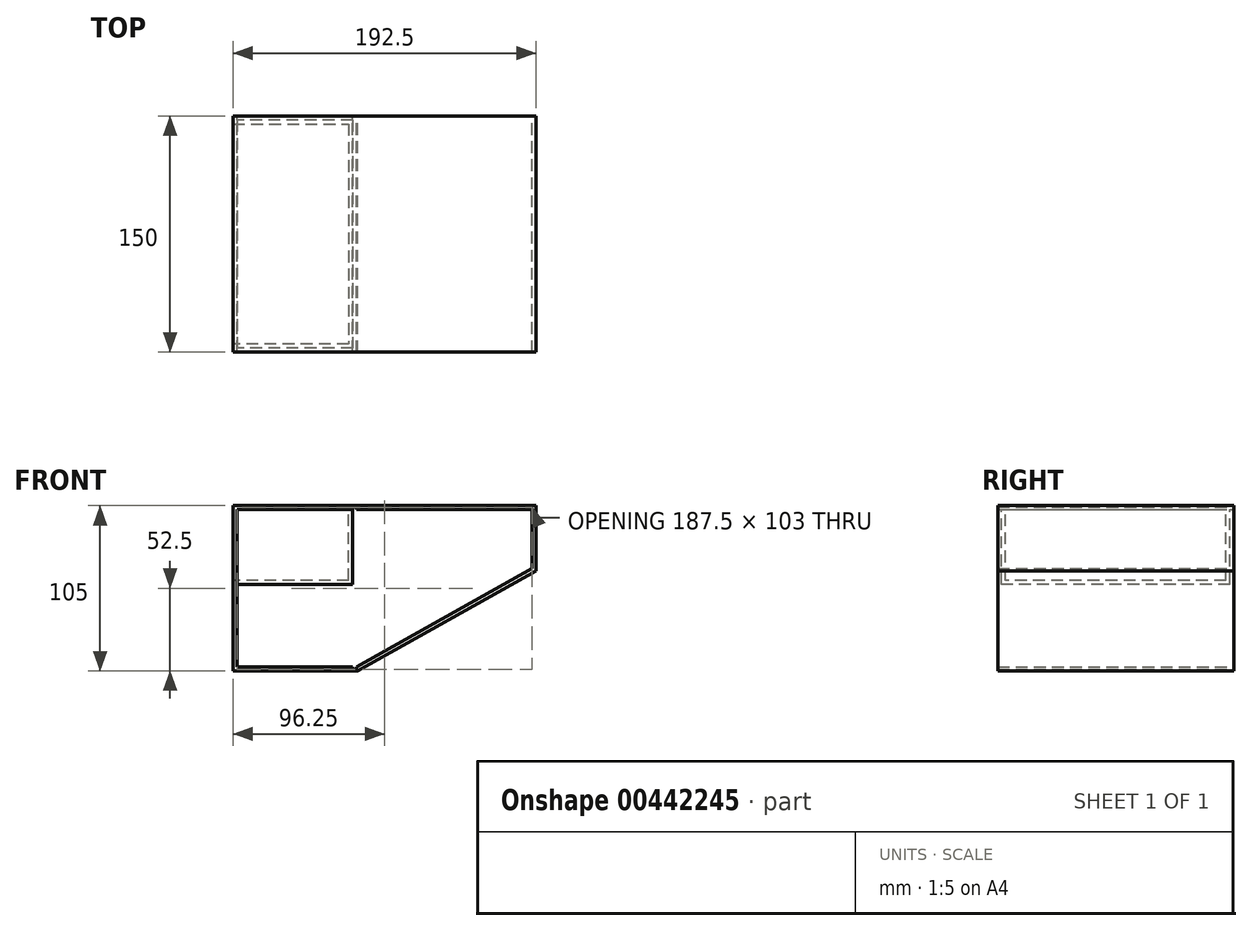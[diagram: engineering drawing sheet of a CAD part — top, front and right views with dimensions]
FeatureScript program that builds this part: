
annotation { "Feature Type Name" : "Feature", "Feature Type Description" : "" }
export const myFeature = defineFeature(function(context is Context, id is Id, definition is map)
    precondition{}
    {
        {
            var Q0;
            Q0=qCreatedBy(makeId("Front.planeOp"),FACE);
            var sketch = newSketch(context, id + "F0", { "sketchPlane" : qUnion([Q0])});
            skLineSegment(sketch, "E0.bottom", {"start": v(-36.5, 50) * mm, "end": v(75, 50) * mm});
            skLineSegment(sketch, "E0.right", {"start": v(75, 50) * mm, "end": v(75, 12.5) * mm});
            skPoint(sketch, "E0.middle", {"position": v(0, 0) * mm});
            skPoint(sketch, "E1.orphan", {"position": v(75, -50) * mm});
            skLineSegment(sketch, "E2", {"start": v(75, 12.5) * mm, "end": v(-36.5, -50) * mm});
            skPoint(sketch, "E3.orphan", {"position": v(-75, 50) * mm});
            skLineSegment(sketch, "E4", {"start": v(-39, -50) * mm, "end": v(-112.5, -50) * mm});
            skLineSegment(sketch, "E5", {"start": v(-112.5, -50) * mm, "end": v(-112.5, 50) * mm});
            skLineSegment(sketch, "E6", {"start": v(-112.5, 50) * mm, "end": v(-39, 50) * mm});
            skLineSegment(sketch, "E7", {"start": v(-112.5, -50) * mm, "end": v(-39, -50) * mm});
            skLineSegment(sketch, "E8.0", {"start": v(77.5, 11.04) * mm, "end": v(-35.85, -52.5) * mm});
            skLineSegment(sketch, "E8.1", {"start": v(77.5, 52.5) * mm, "end": v(77.5, 11.04) * mm});
            skLineSegment(sketch, "E8.2", {"start": v(-115, -52.5) * mm, "end": v(-35.85, -52.5) * mm});
            skLineSegment(sketch, "E8.3", {"start": v(-115, -52.5) * mm, "end": v(-115, 52.5) * mm});
            skLineSegment(sketch, "E8.4", {"start": v(-115, 52.5) * mm, "end": v(-37.5, 52.5) * mm});
            skLineSegment(sketch, "E8.5", {"start": v(-37.5, 52.5) * mm, "end": v(77.5, 52.5) * mm});
            skLineSegment(sketch, "E9.top", {"start": v(-39, -51.5) * mm, "end": v(-36.5, -51.5) * mm});
            skLineSegment(sketch, "E9.left", {"start": v(-39, -50) * mm, "end": v(-39, -51.5) * mm});
            skLineSegment(sketch, "E9.right", {"start": v(-36.5, -50) * mm, "end": v(-36.5, -51.5) * mm});
            skLineSegment(sketch, "E10.top", {"start": v(-39, 51.5) * mm, "end": v(-36.5, 51.5) * mm});
            skLineSegment(sketch, "E10.left", {"start": v(-39, 50) * mm, "end": v(-39, 51.5) * mm});
            skLineSegment(sketch, "E10.right", {"start": v(-36.5, 50) * mm, "end": v(-36.5, 51.5) * mm});
            skSolve(sketch);
        }
        {
            var Q0;
            Q0=makeQuery(id+"F0.imprint","IMPRINT",FACE,{"disambiguationData":[TD([[makeQuery(id+"F0.imprint","IMPRINT",EDGE,{"derivedFrom":sQuery(id+"F0.wireOp",EDGE,"E0.bottom")}),1.0]])]});
            extrude(context, id + "F1", {"entities" : qUnion([Q0]), "depth" : 150 * mm});
        }
        {
            var Q0;
            Q0=makeQuery(id+"F1.opExtrude","SWEPT_FACE",FACE,{"disambiguationData":[OSD([sQuery(id+"F0.wireOp",EDGE,"E8.3")])]});
            var sketch = newSketch(context, id + "F2", { "sketchPlane" : qUnion([Q0])});
            skLineSegment(sketch, "E11", {"start": v(0, 0) * mm, "end": v(150, 0) * mm});
            skLineSegment(sketch, "E12.0", {"start": v(2.5, 2.5) * mm, "end": v(147.5, 2.5) * mm});
            skLineSegment(sketch, "E13.0", {"start": v(147.5, 2.5) * mm, "end": v(147.5, 50) * mm});
            skLineSegment(sketch, "E13.1", {"start": v(147.5, 50) * mm, "end": v(2.5, 50) * mm});
            skLineSegment(sketch, "E14.trimOffspring", {"start": v(2.5, 2.5) * mm, "end": v(2.5, 50) * mm});
            skPoint(sketch, "E15.end.orphan", {"position": v(75, 50) * mm});
            skPoint(sketch, "E15.start.orphan", {"position": v(75, 2.5) * mm});
            skSolve(sketch);
        }
        {
            var Q0;
            Q0 = qSketchRegion(id + "F2", true);
            extrude(context, id + "F3", {"entities" : qUnion([Q0]), "operationType" : NewBodyOperationType.ADD, "oppositeDirection" : true, "depth" : 76 * mm});
        }
        {
            var Q0;
            Q0=makeQuery(id+"F1.opExtrude","SWEPT_FACE",FACE,{"disambiguationData":[OSD([sQuery(id+"F0.wireOp",EDGE,"E8.3")])]});
            shell(context, id + "F4", {"entities" : qUnion([Q0]), "thickness" : 2.5 * mm});
        }
    });
